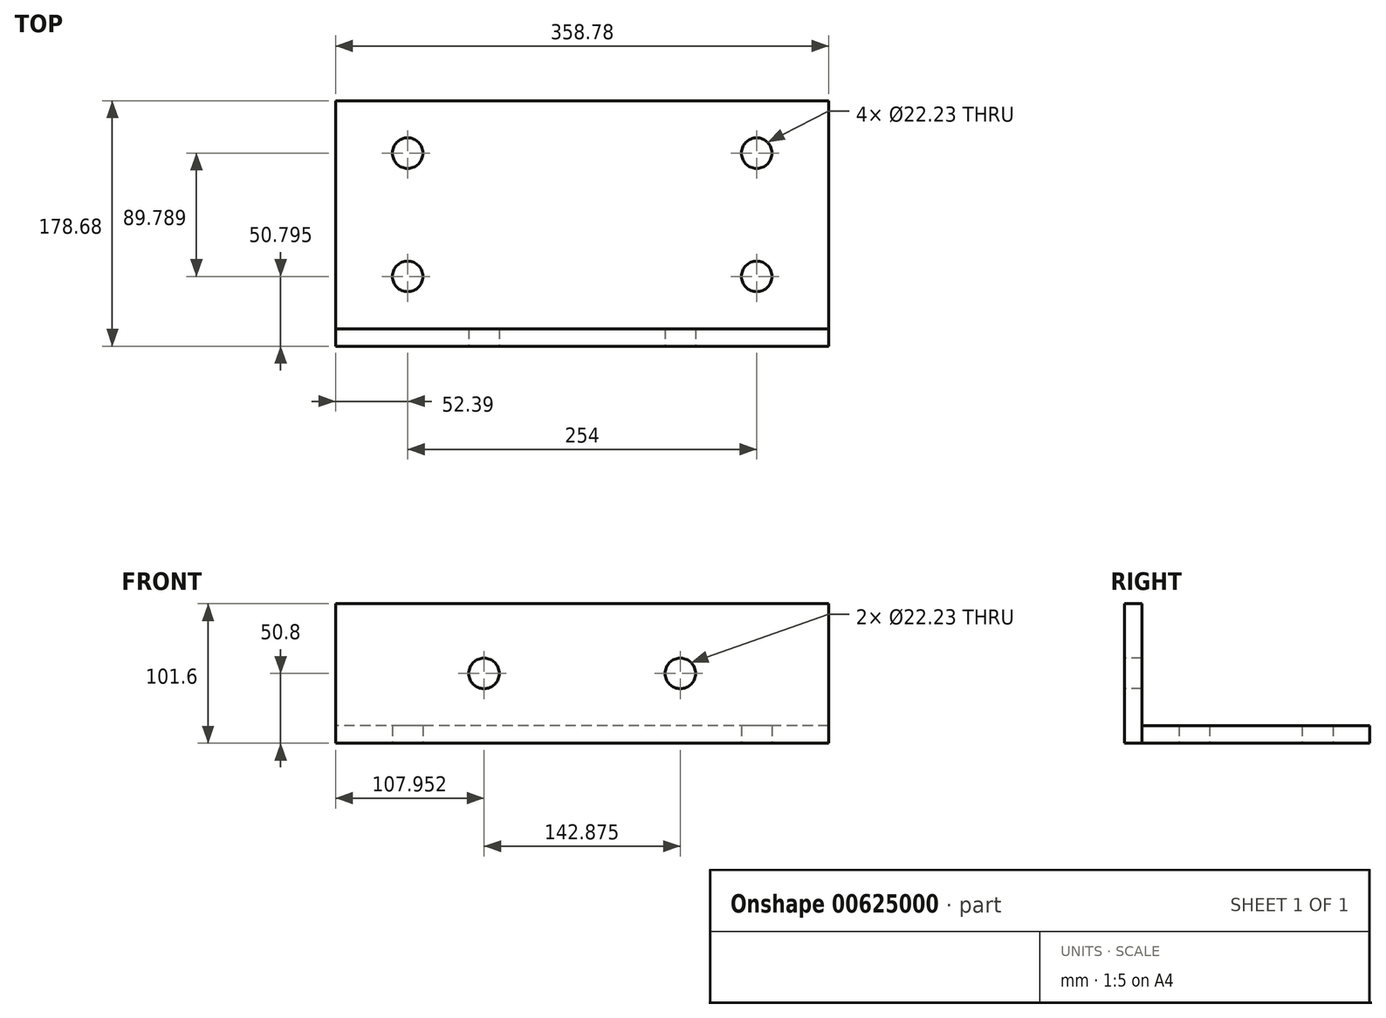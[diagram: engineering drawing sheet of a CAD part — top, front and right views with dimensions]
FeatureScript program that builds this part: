
annotation { "Feature Type Name" : "Feature", "Feature Type Description" : "" }
export const myFeature = defineFeature(function(context is Context, id is Id, definition is map)
    precondition{}
    {
        {
            var Q0;
            Q0=qCreatedBy(makeId("Top.planeOp"),FACE);
            var sketch = newSketch(context, id + "F0", { "sketchPlane" : qUnion([Q0])});
            skLineSegment(sketch, "E0.bottom", {"start": v(179.39, -83) * mm, "end": v(-179.39, -83) * mm});
            skLineSegment(sketch, "E0.top", {"start": v(179.39, 83) * mm, "end": v(-179.39, 83) * mm});
            skLineSegment(sketch, "E0.left", {"start": v(179.39, -83) * mm, "end": v(179.39, 83) * mm});
            skLineSegment(sketch, "E0.right", {"start": v(-179.39, -83) * mm, "end": v(-179.39, 83) * mm});
            skPoint(sketch, "E0.middle", {"position": v(0, 0) * mm});
            skCircle(sketch, "E1", {"center": v(-127, 44.9) * mm, "radius": 11.11 * mm});
            skLineSegment(sketch, "E2", {"start": v(-179.39, 0) * mm, "end": v(179.39, 0) * mm, "construction": true});
            skLineSegment(sketch, "E3", {"start": v(0, 83) * mm, "end": v(0, -83) * mm, "construction": true});
            skCircle(sketch, "E4.MirrorC", {"center": v(127, 44.9) * mm, "radius": 11.11 * mm});
            skCircle(sketch, "E5.MirrorC", {"center": v(-127, -44.9) * mm, "radius": 11.11 * mm});
            skCircle(sketch, "E6.MirrorC", {"center": v(127, -44.9) * mm, "radius": 11.11 * mm});
            skSolve(sketch);
        }
        {
            var Q0;
            Q0 = qSketchRegion(id + "F0", true);
            extrude(context, id + "F1", {"entities" : qUnion([Q0]), "depth" : 12.7 * mm, "offsetDistance" : 25 * mm});
        }
        {
            var Q0;
            Q0=makeQuery(id+"F1.opExtrude","SWEPT_FACE",FACE,{"disambiguationData":[OSD([sQuery(id+"F0.wireOp",EDGE,"E0.bottom")])]});
            var sketch = newSketch(context, id + "F2", { "sketchPlane" : qUnion([Q0])});
            skLineSegment(sketch, "E7.bottom", {"start": v(-179.39, 0) * mm, "end": v(179.39, 0) * mm});
            skLineSegment(sketch, "E7.top", {"start": v(-179.39, 101.6) * mm, "end": v(179.39, 101.6) * mm});
            skLineSegment(sketch, "E7.left", {"start": v(-179.39, 0) * mm, "end": v(-179.39, 101.6) * mm});
            skLineSegment(sketch, "E7.right", {"start": v(179.39, 0) * mm, "end": v(179.39, 101.6) * mm});
            skSolve(sketch);
        }
        {
            var Q0;
            Q0 = qSketchRegion(id + "F2", true);
            extrude(context, id + "F3", {"entities" : qUnion([Q0]), "depth" : 12.7 * mm, "offsetDistance" : 25 * mm});
        }
        {
            var Q0;
            Q0=makeQuery(id+"F3.opExtrude","CAP_FACE",FACE,{"disambiguationData":[OSD([sQuery(id+"F2.wireOp",EDGE,"E7.bottom"),sQuery(id+"F2.wireOp",EDGE,"E7.top"),sQuery(id+"F2.wireOp",EDGE,"E7.left"),sQuery(id+"F2.wireOp",EDGE,"E7.right")])],"isStart":false});
            var sketch = newSketch(context, id + "F4", { "sketchPlane" : qUnion([Q0])});
            skLineSegment(sketch, "E8", {"start": v(0, 0) * mm, "end": v(0, 101.6) * mm, "construction": true});
            skCircle(sketch, "E9", {"center": v(-71.44, 50.8) * mm, "radius": 11.11 * mm});
            skCircle(sketch, "E10.MirrorC", {"center": v(71.44, 50.8) * mm, "radius": 11.11 * mm});
            skSolve(sketch);
        }
        {
            var Q0;
            Q0 = qSketchRegion(id + "F4", true);
            extrude(context, id + "F5", {"entities" : qUnion([Q0]), "operationType" : NewBodyOperationType.REMOVE, "endBound" : BoundingType.THROUGH_ALL, "oppositeDirection" : true, "depth" : 25 * mm, "offsetDistance" : 25 * mm});
        }
    });
